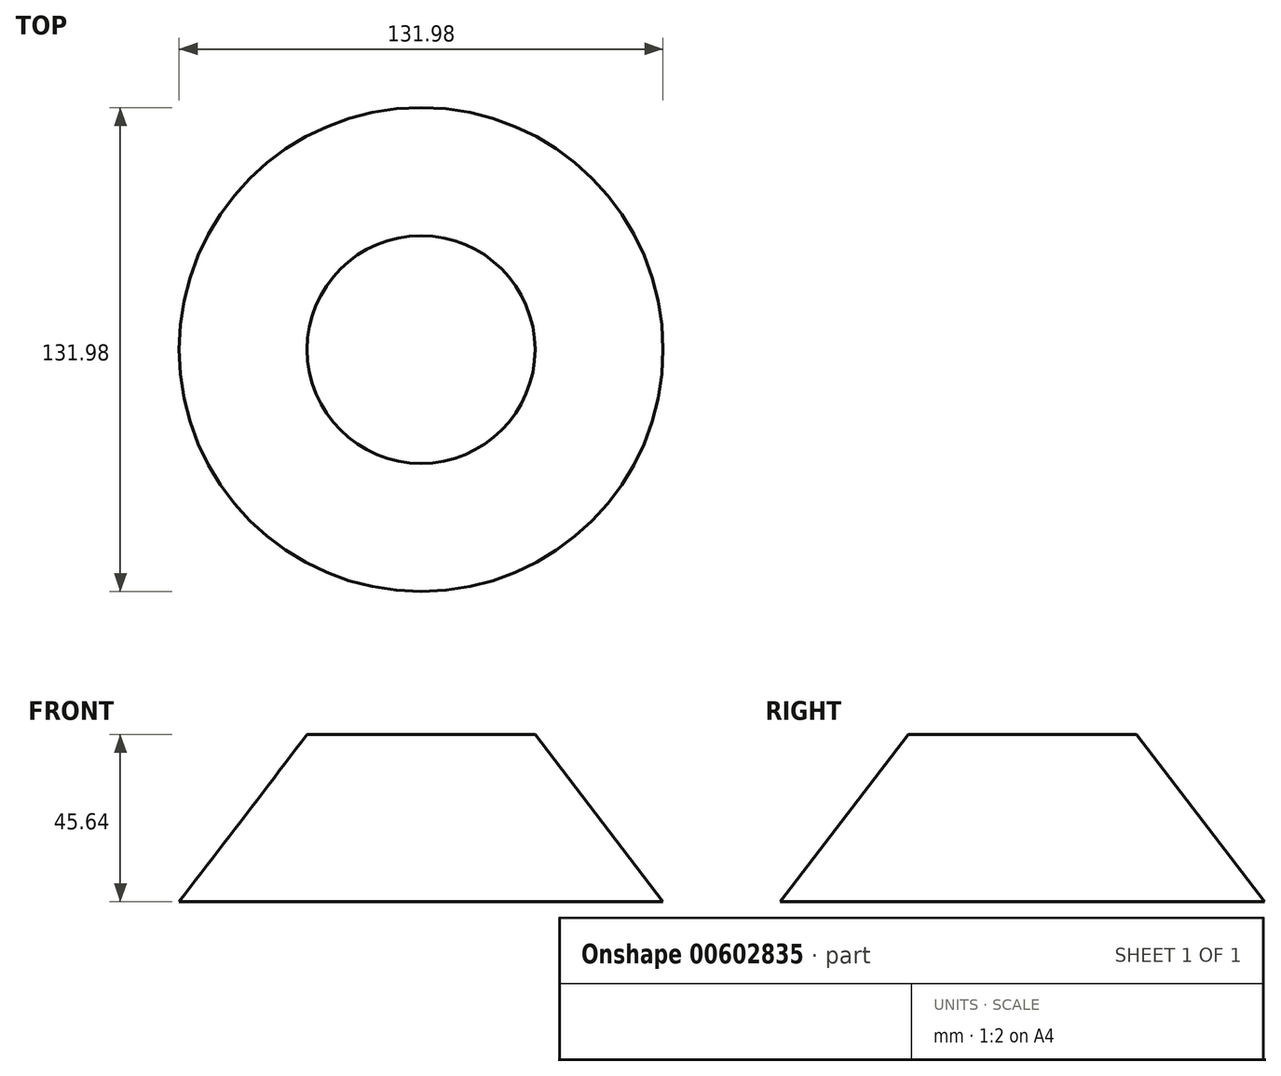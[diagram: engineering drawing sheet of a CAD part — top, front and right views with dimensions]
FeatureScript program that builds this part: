
annotation { "Feature Type Name" : "Feature", "Feature Type Description" : "" }
export const myFeature = defineFeature(function(context is Context, id is Id, definition is map)
    precondition{}
    {
        {
            var Q0;
            Q0=qCreatedBy(makeId("Front.planeOp"),FACE);
            var sketch = newSketch(context, id + "F0", { "sketchPlane" : qUnion([Q0])});
            skLineSegment(sketch, "E0", {"start": v(0, 45.64) * mm, "end": v(31.07, 45.64) * mm});
            skLineSegment(sketch, "E1", {"start": v(31.07, 45.64) * mm, "end": v(66, 0) * mm});
            skLineSegment(sketch, "E2", {"start": v(0, 0) * mm, "end": v(0, 45.64) * mm});
            skLineSegment(sketch, "E3", {"start": v(0, 0) * mm, "end": v(66, 0) * mm});
            skSolve(sketch);
        }
        {
            var Q0;
            Q0=makeQuery(id+"F0.imprint","IMPRINT",FACE,{"disambiguationData":[TD([[makeQuery(id+"F0.imprint","IMPRINT",EDGE,{"derivedFrom":sQuery(id+"F0.wireOp",EDGE,"E0")}),-1.0]])]});
            var Q1;
            Q1=sQuery(id+"F0.wireOp",EDGE,"E2");
            revolve(context, id + "F1", {"entities" : qUnion([Q0]), "axis" : qUnion([Q1]), "revolveType" : RevolveType.FULL});
        }
    });
